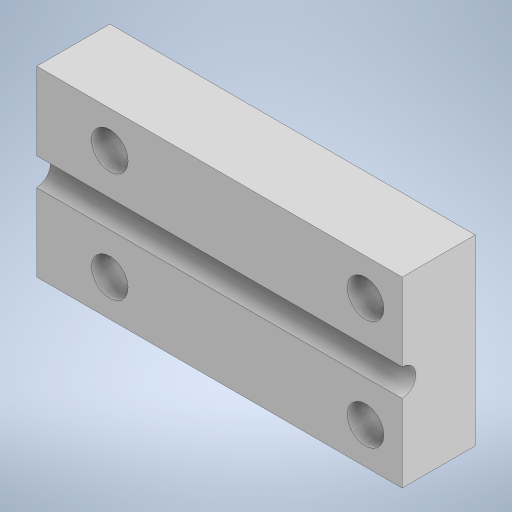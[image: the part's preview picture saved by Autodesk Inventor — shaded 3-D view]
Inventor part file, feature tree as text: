
AUTODESK INVENTOR PART (.ipt)
format: ipt  version: 2024 (Build 280153000, 153)  size: 313,344 bytes
history: native  units: mm
features: extrude x4, sketch x4
ambient origin geometry x8: Origin, YZ Plane, XZ Plane, XY Plane, X Axis, Y Axis, Z Axis, Center Point
bodies: Body1 (feature_tree)
feature tree (8):
  extrude  "Extrusion5"  Depth=1.5mm TaperAngle=0.0deg
  sketch  "Sketch6"
  sketch  "Sketch3"  dims[d5=20.0mm d6=10.0mm d8=0.0mm d9=4.0mm d10=1.5mm d12=0.0mm d13=0.0mm]
  sketch  "Sketch4"  dims[d14=2.0mm d15=2.0mm d16=2.0mm d17=2.0mm d19=0.0mm d20=0.0mm d21=0.5mm d22=0.0mm]
  sketch  "Sketch5"
  extrude  "Extrusion2"  Depth=0.5mm TaperAngle=0.0deg
  extrude  "Extrusion3"  [1 undecoded]
  extrude  "Extrusion4"  [1 undecoded]
note: 2 required parameter values undecoded (feature->parameter linkage not recoverable at this tier; creation-order binding heuristic only, values carry confidence <= 0.55)
